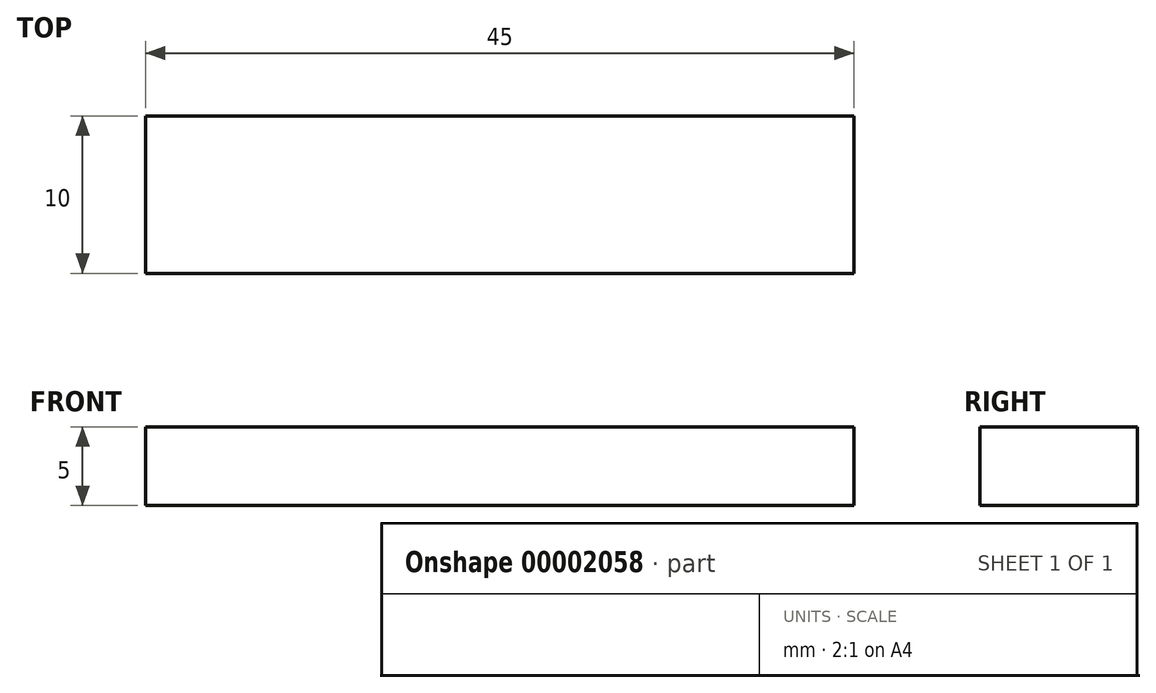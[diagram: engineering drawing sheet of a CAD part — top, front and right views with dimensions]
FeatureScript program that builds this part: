
annotation { "Feature Type Name" : "Feature", "Feature Type Description" : "" }
export const myFeature = defineFeature(function(context is Context, id is Id, definition is map)
    precondition{}
    {
        {
            var Q0;
            Q0=qCreatedBy(makeId("Top.planeOp"),FACE);
            var sketch = newSketch(context, id + "F0", { "sketchPlane" : qUnion([Q0])});
            skLineSegment(sketch, "E0.bottom", {"start": v(-23.29, 17.32) * mm, "end": v(21.71, 17.32) * mm});
            skLineSegment(sketch, "E0.top", {"start": v(-23.29, 27.32) * mm, "end": v(21.71, 27.32) * mm});
            skLineSegment(sketch, "E0.left", {"start": v(-23.29, 17.32) * mm, "end": v(-23.29, 27.32) * mm});
            skLineSegment(sketch, "E0.right", {"start": v(21.71, 17.32) * mm, "end": v(21.71, 27.32) * mm});
            skSolve(sketch);
        }
        {
            var Q0;
            Q0=makeQuery(id+"F0.imprint","IMPRINT",FACE,{"disambiguationData":[TD([[makeQuery(id+"F0.imprint","IMPRINT",EDGE,{"derivedFrom":sQuery(id+"F0.wireOp",EDGE,"E0.bottom")}),1.0]])]});
            extrude(context, id + "F1", {"entities" : qUnion([Q0]), "depth" : 5 * mm});
        }
    });
